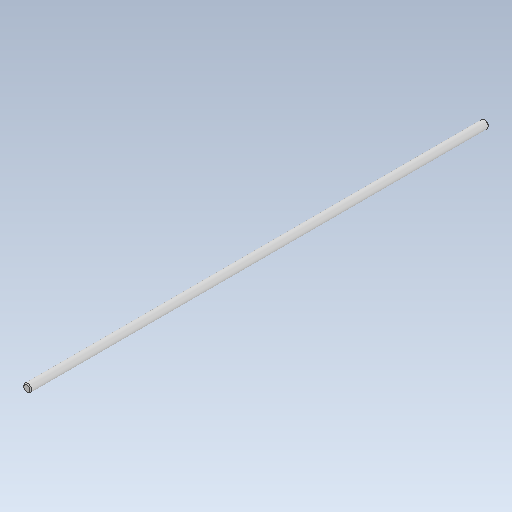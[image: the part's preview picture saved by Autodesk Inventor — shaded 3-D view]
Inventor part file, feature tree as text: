
AUTODESK INVENTOR PART (.ipt)
format: ipt  version: 2020 (Build 240168000, 168)  size: 83,968 bytes
history: native  units: in
note: dims shown in document units (in); Inventor stores cm internally (conversion verified against a paired STEP export)
features: chamfer x1
ambient origin geometry x8: Origin, YZ Plane, XZ Plane, XY Plane, X Axis, Y Axis, Z Axis, Center Point
bodies: Solid1 (feature_tree)
feature tree (1):
  chamfer  "Chamfer1"  [1 undecoded]
note: 1 required parameter value undecoded (feature->parameter linkage not recoverable at this tier; creation-order binding heuristic only, values carry confidence <= 0.55)
